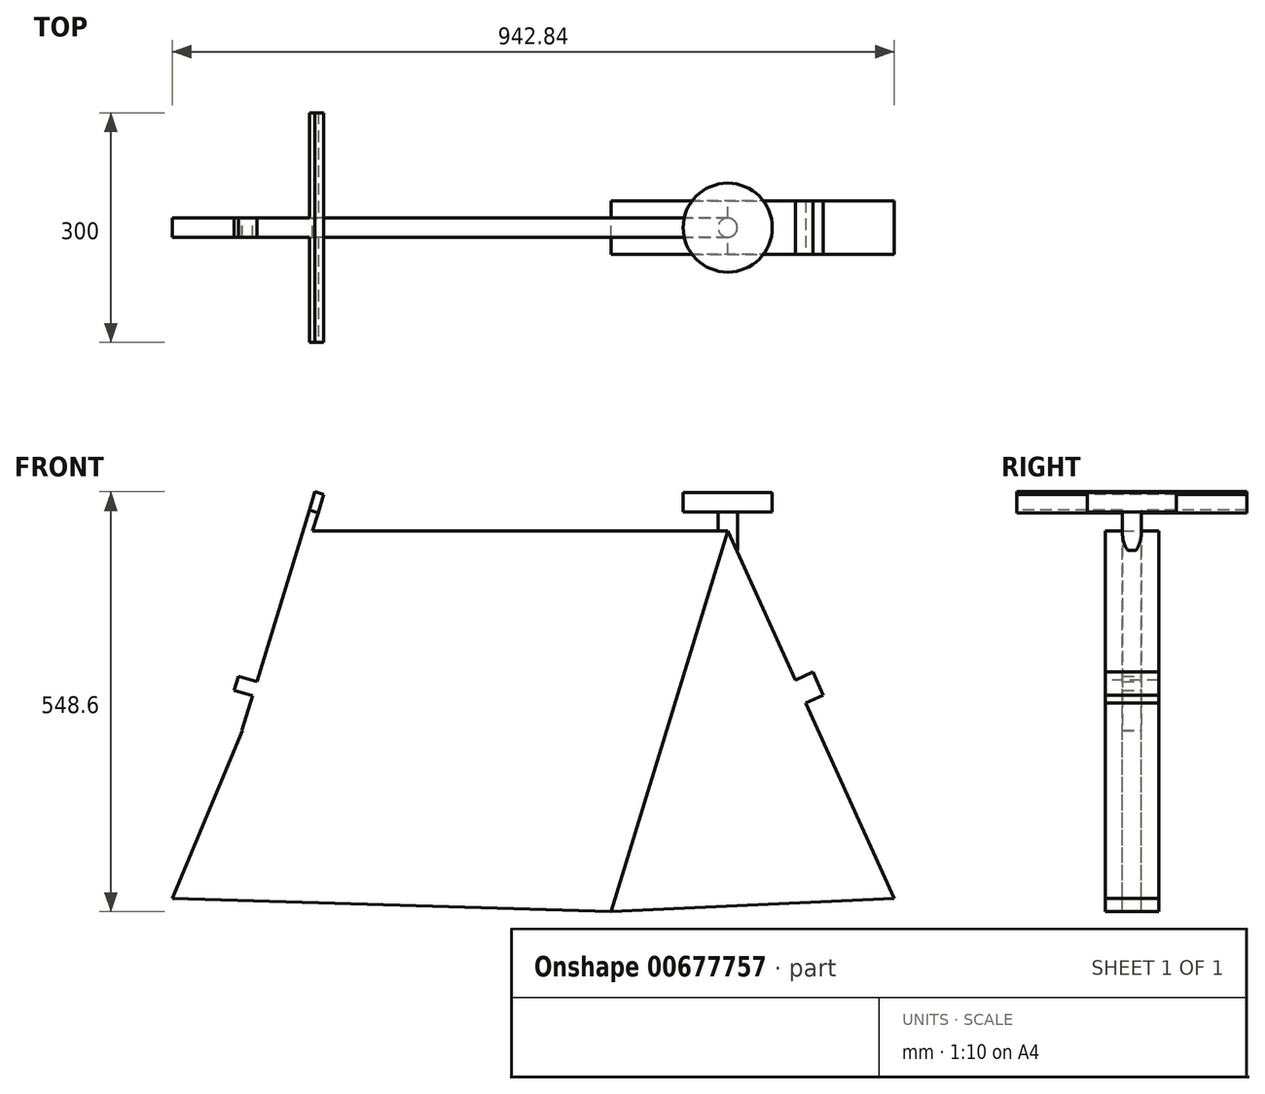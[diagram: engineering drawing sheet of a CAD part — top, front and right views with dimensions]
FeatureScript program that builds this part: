
annotation { "Feature Type Name" : "Feature", "Feature Type Description" : "" }
export const myFeature = defineFeature(function(context is Context, id is Id, definition is map)
    precondition{}
    {
        {
            var Q0;
            Q0=qCreatedBy(makeId("Front.planeOp"),FACE);
            cPlane(context, id + "F0", {"entities" : qUnion([Q0]), "cplaneType" : CPlaneType.OFFSET, "offset" : 100 * mm, "width" : 150 * mm, "height" : 150 * mm});
        }
        {
            var Q0;
            Q0=qCreatedBy(id+"F0.planeOp",FACE);
            var sketch = newSketch(context, id + "F1", { "sketchPlane" : qUnion([Q0])});
            skLineSegment(sketch, "E0", {"start": v(-699.2, -92.54) * mm, "end": v(700.8, -92.54) * mm, "construction": true});
            skLineSegment(sketch, "E1", {"start": v(-699.2, 184.46) * mm, "end": v(700.8, 184.46) * mm, "construction": true});
            skLineSegment(sketch, "E2", {"start": v(-699.2, 201.96) * mm, "end": v(700.8, 201.96) * mm, "construction": true});
            skLineSegment(sketch, "E3", {"start": v(0, -112.8) * mm, "end": v(0, 476.43) * mm, "construction": true});
            skLineSegment(sketch, "E4", {"start": v(0, 184.46) * mm, "end": v(152.03, 681.74) * mm});
            skLineSegment(sketch, "E5", {"start": v(152.03, 681.74) * mm, "end": v(-389.97, 681.74) * mm});
            skLineSegment(sketch, "E6", {"start": v(-389.97, 681.74) * mm, "end": v(-436.75, 528.73) * mm});
            skLineSegment(sketch, "E7", {"start": v(-436.75, 528.73) * mm, "end": v(-640.72, -138.44) * mm, "construction": true});
            skLineSegment(sketch, "E8", {"start": v(-488.06, 480.61) * mm, "end": v(-614.29, 67.73) * mm, "construction": true});
            skPoint(sketch, "E9", {"position": v(-573.25, 201.96) * mm});
            skCircle(sketch, "E10", {"center": v(-573.25, 201.96) * mm, "radius": 294.5 * mm});
            skLineSegment(sketch, "E11", {"start": v(0, 184.46) * mm, "end": v(47.84, 184.46) * mm});
            skLineSegment(sketch, "E12", {"start": v(369.59, 201.96) * mm, "end": v(0, 184.46) * mm});
            skCircle(sketch, "E13", {"center": v(369.59, 201.96) * mm, "radius": 294.5 * mm});
            skLineSegment(sketch, "E14", {"start": v(152.03, 681.74) * mm, "end": v(369.59, 201.96) * mm});
            skLineSegment(sketch, "E15", {"start": v(-436.75, 528.73) * mm, "end": v(0, 184.46) * mm});
            skLineSegment(sketch, "E16", {"start": v(-573.25, 201.96) * mm, "end": v(-573.25, -166.77) * mm, "construction": true});
            skPoint(sketch, "E17", {"position": v(-626.69, -92.54) * mm});
            skPoint(sketch, "E18", {"position": v(-573.25, -92.54) * mm});
            skPoint(sketch, "E19", {"position": v(0, 184.46) * mm});
            skPoint(sketch, "E20", {"position": v(75.6, 184.46) * mm});
            skLineSegment(sketch, "E21", {"start": v(0, 184.46) * mm, "end": v(-573.25, 201.96) * mm});
            skLineSegment(sketch, "E22", {"start": v(-573.25, 201.96) * mm, "end": v(-436.75, 528.73) * mm});
            skSolve(sketch);
        }
        {
            var Q0;
            Q0=makeQuery(id+"F1.imprint","IMPRINT",FACE,{"disambiguationData":[TD([[makeQuery(id+"F1.imprint","IMPRINT",EDGE,{"derivedFrom":sQuery(id+"F1.wireOp",EDGE,"E4")}),1.0]])]});
            extrude(context, id + "F2", {"entities" : qUnion([Q0]), "endBound" : BoundingType.SYMMETRIC, "depth" : 25 * mm, "offsetDistance" : 25 * mm});
        }
        {
            var Q0;
            {var subQ0=sQuery(id+"F1.wireOp",EDGE,"E4");Q0=makeQuery(id+"F1.imprint","IMPRINT",FACE,{"disambiguationData":[TD([[makeQuery(id+"F1.imprint","IMPRINT",EDGE,{"derivedFrom":subQ0}),-1.0]])]});}
            var Q1;
            {var subQ0=sQuery(id+"F1.wireOp",EDGE,"E13");var subQ1=sQuery(id+"F1.wireOp",EDGE,"E12");var subQ2=makeQuery(id+"F1.imprint","INTERSECT",VERTEX,{"derivedFrom":[subQ1,subQ0]});Q1=makeQuery(id+"F1.imprint","IMPRINT",FACE,{"disambiguationData":[TD([[makeQuery(id+"F1.imprint","IMPRINT",EDGE,{"disambiguationData":[TD([[subQ2,1.0]])],"derivedFrom":subQ1}),-1.0]])]});}
            extrude(context, id + "F3", {"entities" : qUnion([Q0, Q1]), "operationType" : NewBodyOperationType.ADD, "endBound" : BoundingType.SYMMETRIC, "depth" : 70 * mm, "offsetDistance" : 25 * mm});
        }
        {
            var Q0;
            Q0=makeQuery(id+"F2.opExtrude","SWEPT_FACE",FACE,{"disambiguationData":[OSD([sQuery(id+"F1.wireOp",EDGE,"E5")])]});
            var sketch = newSketch(context, id + "F4", { "sketchPlane" : qUnion([Q0])});
            skCircle(sketch, "E23", {"center": v(152.03, -100) * mm, "radius": 12.5 * mm});
            skSolve(sketch);
        }
        {
            var Q0;
            {var subQ1=sQuery(id+"F1.wireOp",EDGE,"E14");var subQ2=sQuery(id+"F1.wireOp",EDGE,"E5");var subQ3=sQuery(id+"F1.wireOp",EDGE,"E4");var subQ4=makeQuery(id+"F3.boolean.opBoolean","MERGE",EDGE,{"derivedFrom":[makeQuery(id+"F2.opExtrude","SWEPT_EDGE",EDGE,{"disambiguationData":[OSD([subQ3,subQ2,subQ1])]}),makeQuery(id+"F3.opExtrude","SWEPT_EDGE",EDGE,{"disambiguationData":[OSD([subQ3,subQ2,subQ1])]})]});Q0=makeQuery(id+"F4.imprint","IMPRINT",FACE,{"disambiguationData":[TD([[makeQuery(id+"F4.imprint","IMPRINT",EDGE,{"derivedFrom":subQ4}),1.0]])]});}
            var Q1;
            {var subQ1=sQuery(id+"F1.wireOp",EDGE,"E14");var subQ2=sQuery(id+"F1.wireOp",EDGE,"E5");var subQ3=sQuery(id+"F1.wireOp",EDGE,"E4");var subQ4=makeQuery(id+"F3.boolean.opBoolean","MERGE",EDGE,{"derivedFrom":[makeQuery(id+"F2.opExtrude","SWEPT_EDGE",EDGE,{"disambiguationData":[OSD([subQ3,subQ2,subQ1])]}),makeQuery(id+"F3.opExtrude","SWEPT_EDGE",EDGE,{"disambiguationData":[OSD([subQ3,subQ2,subQ1])]})]});Q1=makeQuery(id+"F4.imprint","IMPRINT",FACE,{"disambiguationData":[TD([[makeQuery(id+"F4.imprint","IMPRINT",EDGE,{"derivedFrom":subQ4}),-1.0]])]});}
            extrude(context, id + "F5", {"entities" : qUnion([Q0, Q1]), "operationType" : NewBodyOperationType.ADD, "endBound" : BoundingType.SYMMETRIC, "depth" : 50 * mm, "offsetDistance" : 25 * mm});
        }
        {
            var Q0;
            Q0=makeQuery(id+"F2.opExtrude","SWEPT_FACE",FACE,{"disambiguationData":[OSD([sQuery(id+"F1.wireOp",EDGE,"E6")])]});
            extrude(context, id + "F6", {"entities" : qUnion([Q0]), "operationType" : NewBodyOperationType.ADD, "depth" : 12 * mm, "offsetDistance" : 25 * mm});
        }
        {
            var Q0;
            Q0=makeQuery(id+"F6.opExtrude","SWEPT_FACE",FACE,{"disambiguationData":[OSD([sQuery(id+"F1.wireOp",EDGE,"E6"),sQuery(id+"F1.wireOp",EDGE,"E15")])]});
            extrude(context, id + "F7", {"entities" : qUnion([Q0]), "operationType" : NewBodyOperationType.ADD, "depth" : 116 * mm, "offsetDistance" : 25 * mm, "hasSecondDirection" : true, "secondDirectionOppositeDirection" : true, "secondDirectionDepth" : 25 * mm});
        }
        {
            var Q0;
            Q0=makeQuery(id+"F6.opExtrude","SWEPT_FACE",FACE,{"disambiguationData":[OSD([sQuery(id+"F1.wireOp",EDGE,"E5"),sQuery(id+"F1.wireOp",EDGE,"E6")])]});
            extrude(context, id + "F8", {"entities" : qUnion([Q0]), "operationType" : NewBodyOperationType.ADD, "depth" : 25 * mm, "offsetDistance" : 25 * mm});
        }
        {
            var Q0;
            Q0=makeQuery(id+"F8.opExtrude","CAP_FACE",FACE,{"disambiguationData":[OSD([sQuery(id+"F1.wireOp",EDGE,"E5"),sQuery(id+"F1.wireOp",EDGE,"E6")])],"isStart":false});
            var sketch = newSketch(context, id + "F9", { "sketchPlane" : qUnion([Q0])});
            skPoint(sketch, "E24", {"position": v(-578.25, -100) * mm});
            skPoint(sketch, "E24.positionSnap0", {"position": v(-572.25, -100) * mm});
            skLineSegment(sketch, "E25.bottom", {"start": v(-572.25, 50) * mm, "end": v(-584.25, 50) * mm});
            skLineSegment(sketch, "E25.top", {"start": v(-572.25, -250) * mm, "end": v(-584.25, -250) * mm});
            skLineSegment(sketch, "E25.left", {"start": v(-572.25, 50) * mm, "end": v(-572.25, -250) * mm});
            skLineSegment(sketch, "E25.right", {"start": v(-584.25, 50) * mm, "end": v(-584.25, -250) * mm});
            skSolve(sketch);
        }
        {
            var Q0;
            {var subQ0=sQuery(id+"F9.wireOp",EDGE,"E25.top");Q0=makeQuery(id+"F9.imprint","IMPRINT",FACE,{"disambiguationData":[TD([[makeQuery(id+"F9.imprint","IMPRINT",EDGE,{"derivedFrom":subQ0}),-1.0]])]});}
            var Q1;
            {var subQ0=sQuery(id+"F9.wireOp",EDGE,"E25.bottom");Q1=makeQuery(id+"F9.imprint","IMPRINT",FACE,{"disambiguationData":[TD([[makeQuery(id+"F9.imprint","IMPRINT",EDGE,{"derivedFrom":subQ0}),1.0]])]});}
            var Q2;
            {var subQ1=sQuery(id+"F1.wireOp",EDGE,"E6");var subQ2=sQuery(id+"F1.wireOp",EDGE,"E5");var subQ3=makeQuery(id+"F8.opExtrude","CAP_EDGE",EDGE,{"disambiguationData":[OSD([subQ2,subQ1]),TDD([makeQuery(id+"F6.opExtrude","SWEPT_EDGE",EDGE,{"disambiguationData":[OSD([subQ2,subQ1]),TDD([makeQuery(id+"F2.opExtrude","CAP_VERTEX",VERTEX,{"disambiguationData":[OSD([subQ2,subQ1])],"isStart":true})])]})])],"isStart":false});Q2=makeQuery(id+"F9.imprint","IMPRINT",FACE,{"disambiguationData":[TD([[makeQuery(id+"F9.imprint","IMPRINT",EDGE,{"derivedFrom":subQ3}),-1.0]])]});}
            extrude(context, id + "F10", {"entities" : qUnion([Q0, Q1, Q2]), "operationType" : NewBodyOperationType.ADD, "depth" : 25 * mm, "offsetDistance" : 25 * mm});
        }
        {
            var Q0;
            Q0=makeQuery(id+"F3.opExtrude","SWEPT_FACE",FACE,{"disambiguationData":[OSD([sQuery(id+"F1.wireOp",EDGE,"E14")])]});
            var sketch = newSketch(context, id + "F11", { "sketchPlane" : qUnion([Q0])});
            skPoint(sketch, "E26", {"position": v(-100, 327.76) * mm});
            skLineSegment(sketch, "E27.bottom", {"start": v(-65, 311.16) * mm, "end": v(-135, 311.16) * mm});
            skLineSegment(sketch, "E27.top", {"start": v(-65, 344.37) * mm, "end": v(-135, 344.37) * mm});
            skLineSegment(sketch, "E27.left", {"start": v(-65, 311.16) * mm, "end": v(-65, 344.37) * mm});
            skLineSegment(sketch, "E27.right", {"start": v(-135, 311.16) * mm, "end": v(-135, 344.37) * mm});
            skSolve(sketch);
        }
        {
            var Q0;
            Q0=makeQuery(id+"F11.imprint","IMPRINT",FACE,{"disambiguationData":[TD([[makeQuery(id+"F11.imprint","IMPRINT",EDGE,{"derivedFrom":sQuery(id+"F11.wireOp",EDGE,"E27.bottom")}),-1.0]])]});
            extrude(context, id + "F12", {"entities" : qUnion([Q0]), "operationType" : NewBodyOperationType.ADD, "depth" : 25 * mm, "offsetDistance" : 25 * mm});
        }
        {
            var Q0;
            {var subQ0=sQuery(id+"F1.wireOp",EDGE,"E21");var subQ1=sQuery(id+"F1.wireOp",EDGE,"E10");var subQ2=makeQuery(id+"F1.imprint","INTERSECT",VERTEX,{"derivedFrom":[subQ1,subQ0]});Q0=makeQuery(id+"F1.imprint","IMPRINT",FACE,{"disambiguationData":[TD([[makeQuery(id+"F1.imprint","IMPRINT",EDGE,{"disambiguationData":[TD([[subQ2,-1.0]])],"derivedFrom":subQ1}),1.0]])]});}
            var Q1;
            {var subQ5=sQuery(id+"F1.wireOp",EDGE,"E15");Q1=makeQuery(id+"F1.imprint","IMPRINT",FACE,{"disambiguationData":[TD([[makeQuery(id+"F1.imprint","IMPRINT",EDGE,{"derivedFrom":subQ5}),-1.0]])]});}
            extrude(context, id + "F13", {"entities" : qUnion([Q0, Q1]), "operationType" : NewBodyOperationType.ADD, "endBound" : BoundingType.SYMMETRIC, "depth" : 25 * mm, "offsetDistance" : 25 * mm});
        }
        {
            var Q0;
            {var subQ0=sQuery(id+"F1.wireOp",EDGE,"E6");var subQ1=sQuery(id+"F1.wireOp",EDGE,"E5");var subQ2=sQuery(id+"F1.wireOp",EDGE,"E22");var subQ3=sQuery(id+"F1.wireOp",EDGE,"E15");Q0=makeQuery(id+"F10.boolean.opBoolean","MERGE",FACE,{"derivedFrom":[makeQuery(id+"F8.boolean.opBoolean","MERGE",FACE,{"derivedFrom":[makeQuery(id+"F7.boolean.opBoolean","MERGE",FACE,{"derivedFrom":[makeQuery(id+"F6.opExtrude","CAP_FACE",FACE,{"disambiguationData":[OSD([subQ0])],"isStart":false}),makeQuery(id+"F7.opExtrude","SWEPT_FACE",FACE,{"disambiguationData":[OSD([subQ0,subQ3,subQ2]),TDD([makeQuery(id+"F6.opExtrude","CAP_EDGE",EDGE,{"disambiguationData":[OSD([subQ0,subQ3,subQ2])],"isStart":false})])]})]}),makeQuery(id+"F8.opExtrude","SWEPT_FACE",FACE,{"disambiguationData":[OSD([subQ1,subQ0]),TDD([makeQuery(id+"F6.opExtrude","CAP_EDGE",EDGE,{"disambiguationData":[OSD([subQ1,subQ0])],"isStart":false})])]})]}),makeQuery(id+"F10.opExtrude","SWEPT_FACE",FACE,{"disambiguationData":[OSD([sQuery(id+"F9.wireOp",EDGE,"E25.right")])]})]});}
            var sketch = newSketch(context, id + "F14", { "sketchPlane" : qUnion([Q0])});
            skPoint(sketch, "E28", {"position": v(100, 318.75) * mm});
            skLineSegment(sketch, "E29.bottom", {"start": v(112.5, 328.5) * mm, "end": v(87.5, 328.5) * mm});
            skLineSegment(sketch, "E29.top", {"start": v(112.5, 308.99) * mm, "end": v(87.5, 308.99) * mm});
            skLineSegment(sketch, "E29.left", {"start": v(112.5, 328.5) * mm, "end": v(112.5, 308.99) * mm});
            skLineSegment(sketch, "E29.right", {"start": v(87.5, 328.5) * mm, "end": v(87.5, 308.99) * mm});
            skSolve(sketch);
        }
        {
            var Q0;
            Q0=makeQuery(id+"F14.imprint","IMPRINT",FACE,{"disambiguationData":[TD([[makeQuery(id+"F14.imprint","IMPRINT",EDGE,{"derivedFrom":sQuery(id+"F14.wireOp",EDGE,"E29.bottom")}),1.0]])]});
            extrude(context, id + "F15", {"entities" : qUnion([Q0]), "operationType" : NewBodyOperationType.ADD, "depth" : 25 * mm, "offsetDistance" : 25 * mm});
        }
        {
            var Q0;
            Q0=makeQuery(id+"F5.opExtrude","CAP_FACE",FACE,{"disambiguationData":[OSD([sQuery(id+"F4.wireOp",EDGE,"E23")])],"isStart":false});
            var sketch = newSketch(context, id + "F16", { "sketchPlane" : qUnion([Q0])});
            skCircle(sketch, "E30", {"center": v(152.03, -100) * mm, "radius": 56.32 * mm});
            skSolve(sketch);
        }
        {
            var Q0;
            Q0=makeQuery(id+"F16.imprint","IMPRINT",FACE,{"disambiguationData":[TD([[makeQuery(id+"F16.imprint","IMPRINT",EDGE,{"derivedFrom":sQuery(id+"F16.wireOp",EDGE,"E30")}),1.0]])]});
            extrude(context, id + "F17", {"entities" : qUnion([Q0]), "depth" : 25 * mm, "offsetDistance" : 25 * mm});
        }
        {
            var Q0;
            Q0=makeQuery(id+"F17.opExtrude","SWEPT_BODY",BODY,{"disambiguationData":[OSD([sQuery(id+"F4.wireOp",EDGE,"E23"),sQuery(id+"F16.wireOp",EDGE,"E30")])]});
            deleteBodies(context, id + "F18", {"entities" : qUnion([Q0])});
        }
        {
            var Q0;
            Q0=makeQuery(id+"F5.opExtrude","CAP_FACE",FACE,{"disambiguationData":[OSD([sQuery(id+"F4.wireOp",EDGE,"E23")])],"isStart":false});
            var sketch = newSketch(context, id + "F19", { "sketchPlane" : qUnion([Q0])});
            skCircle(sketch, "E31", {"center": v(152.03, -100) * mm, "radius": 58.14 * mm});
            skSolve(sketch);
        }
        {
            var Q0;
            Q0 = qSketchRegion(id + "F19", true);
            extrude(context, id + "F20", {"entities" : qUnion([Q0]), "operationType" : NewBodyOperationType.ADD, "depth" : 25 * mm, "offsetDistance" : 25 * mm});
        }
    });
